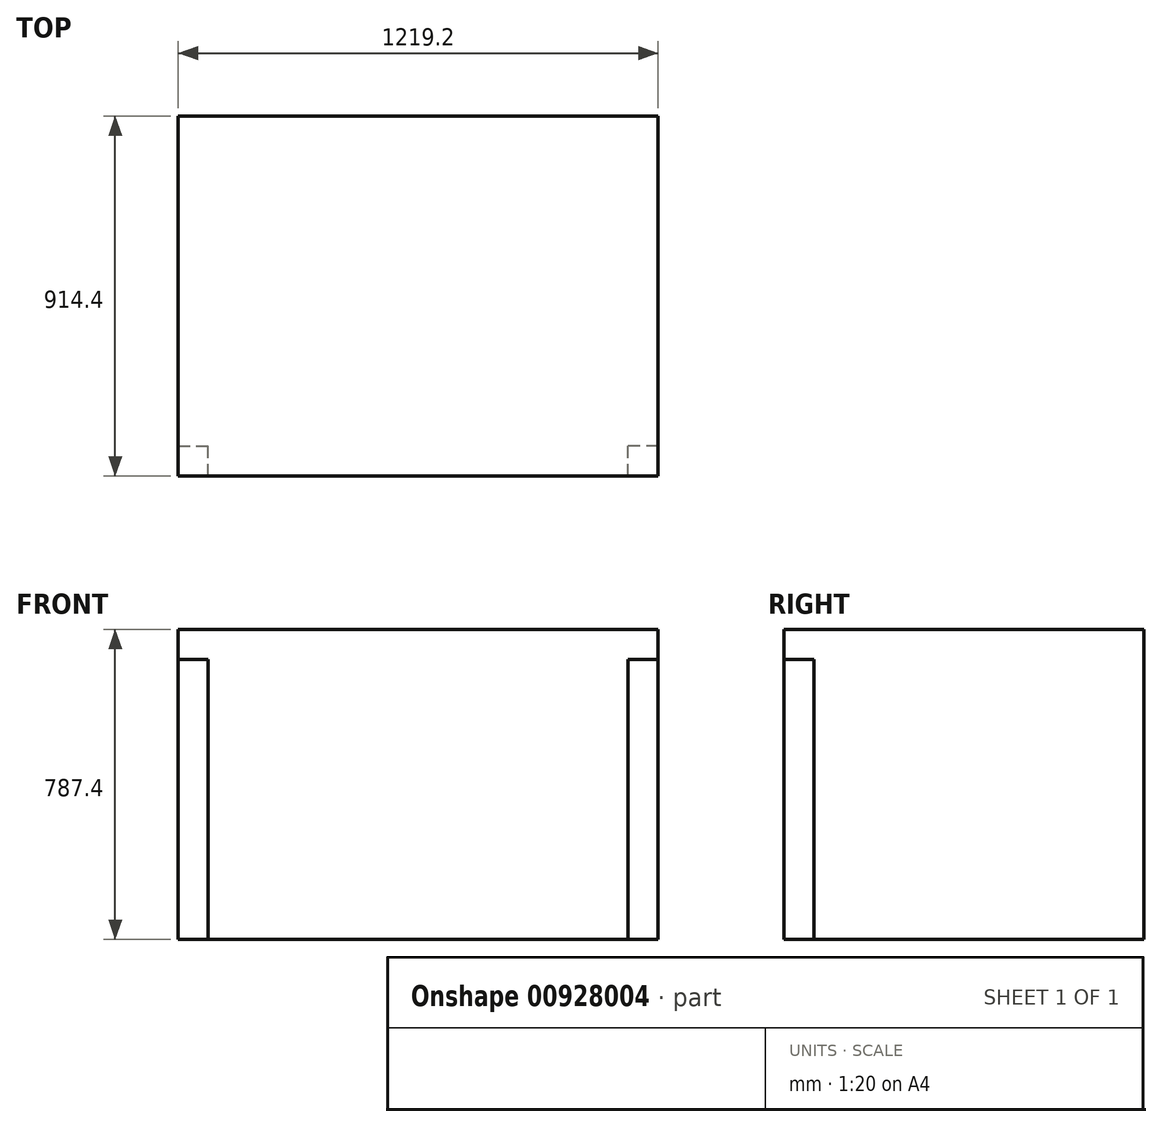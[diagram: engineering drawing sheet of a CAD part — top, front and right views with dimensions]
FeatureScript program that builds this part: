
annotation { "Feature Type Name" : "Feature", "Feature Type Description" : "" }
export const myFeature = defineFeature(function(context is Context, id is Id, definition is map)
    precondition{}
    {
        {
            var Q0;
            Q0=qCreatedBy(makeId("Top.planeOp"),FACE);
            var sketch = newSketch(context, id + "F0", { "sketchPlane" : qUnion([Q0])});
            skLineSegment(sketch, "E0.bottom", {"start": v(609.6, -457.2) * mm, "end": v(-609.6, -457.2) * mm});
            skLineSegment(sketch, "E0.top", {"start": v(609.6, 457.2) * mm, "end": v(-609.6, 457.2) * mm});
            skLineSegment(sketch, "E0.left", {"start": v(609.6, -457.2) * mm, "end": v(609.6, 457.2) * mm});
            skLineSegment(sketch, "E0.right", {"start": v(-609.6, -457.2) * mm, "end": v(-609.6, 457.2) * mm});
            skPoint(sketch, "E0.middle", {"position": v(0, 0) * mm});
            skSolve(sketch);
        }
        {
            var Q0;
            Q0 = qSketchRegion(id + "F0", true);
            extrude(context, id + "F1", {"entities" : qUnion([Q0]), "depth" : 787.4 * mm, "offsetDistance" : 25.4 * mm});
        }
        {
            var Q0;
            Q0=makeQuery(id+"F1.opExtrude","CAP_FACE",FACE,{"disambiguationData":[OSD([sQuery(id+"F0.wireOp",EDGE,"E0.bottom"),sQuery(id+"F0.wireOp",EDGE,"E0.top"),sQuery(id+"F0.wireOp",EDGE,"E0.left"),sQuery(id+"F0.wireOp",EDGE,"E0.right")])],"isStart":true});
            var sketch = newSketch(context, id + "F2", { "sketchPlane" : qUnion([Q0])});
            skLineSegment(sketch, "E1.bottom", {"start": v(-609.6, 457.2) * mm, "end": v(609.6, 457.2) * mm});
            skLineSegment(sketch, "E1.top", {"start": v(-609.6, -457.2) * mm, "end": v(609.6, -457.2) * mm});
            skLineSegment(sketch, "E1.left", {"start": v(-609.6, 457.2) * mm, "end": v(-609.6, -457.2) * mm});
            skLineSegment(sketch, "E1.right", {"start": v(609.6, 457.2) * mm, "end": v(609.6, -457.2) * mm});
            skLineSegment(sketch, "E2.bottom", {"start": v(-609.6, 457.2) * mm, "end": v(-533.4, 457.2) * mm});
            skLineSegment(sketch, "E2.top", {"start": v(-609.6, 381) * mm, "end": v(-533.4, 381) * mm});
            skLineSegment(sketch, "E2.left", {"start": v(-609.6, 457.2) * mm, "end": v(-609.6, 381) * mm});
            skLineSegment(sketch, "E2.right", {"start": v(-533.4, 457.2) * mm, "end": v(-533.4, 381) * mm});
            skLineSegment(sketch, "E3.MirrorCS", {"start": v(609.6, 381) * mm, "end": v(533.4, 381) * mm});
            skLineSegment(sketch, "E4.MirrorCS", {"start": v(609.6, 457.2) * mm, "end": v(609.6, 381) * mm});
            skLineSegment(sketch, "E5.MirrorCS", {"start": v(533.4, 457.2) * mm, "end": v(533.4, 381) * mm});
            skLineSegment(sketch, "E6.MirrorCS", {"start": v(609.6, 457.2) * mm, "end": v(533.4, 457.2) * mm});
            skLineSegment(sketch, "E7.MirrorCS", {"start": v(-609.6, -381) * mm, "end": v(-533.4, -381) * mm});
            skLineSegment(sketch, "E8.MirrorCS", {"start": v(-533.4, -457.2) * mm, "end": v(-533.4, -381) * mm});
            skLineSegment(sketch, "E9.MirrorCS", {"start": v(533.4, -457.2) * mm, "end": v(533.4, -381) * mm});
            skLineSegment(sketch, "E10.MirrorCS", {"start": v(-609.6, -457.2) * mm, "end": v(-533.4, -457.2) * mm});
            skLineSegment(sketch, "E11.MirrorCS", {"start": v(-609.6, -457.2) * mm, "end": v(-609.6, -381) * mm});
            skLineSegment(sketch, "E12.MirrorCS", {"start": v(609.6, -457.2) * mm, "end": v(609.6, -381) * mm});
            skLineSegment(sketch, "E13.MirrorCS", {"start": v(609.6, -457.2) * mm, "end": v(533.4, -457.2) * mm});
            skLineSegment(sketch, "E14.MirrorCS", {"start": v(609.6, -381) * mm, "end": v(533.4, -381) * mm});
            skLineSegment(sketch, "E15.MirrorCS", {"start": v(609.6, -457.2) * mm, "end": v(609.6, 457.2) * mm});
            skSolve(sketch);
        }
        {
            var Q0;
            Q0=makeQuery(id+"F2.imprint","IMPRINT",FACE,{"disambiguationData":[TD([[makeQuery(id+"F2.imprint","IMPRINT",EDGE,{"derivedFrom":sQuery(id+"F2.wireOp",EDGE,"E1.bottom")}),1.0]])]});
            extrude(context, id + "F3", {"entities" : qUnion([Q0]), "operationType" : NewBodyOperationType.REMOVE, "oppositeDirection" : true, "depth" : 711.2 * mm, "offsetDistance" : 25.4 * mm});
        }
    });
